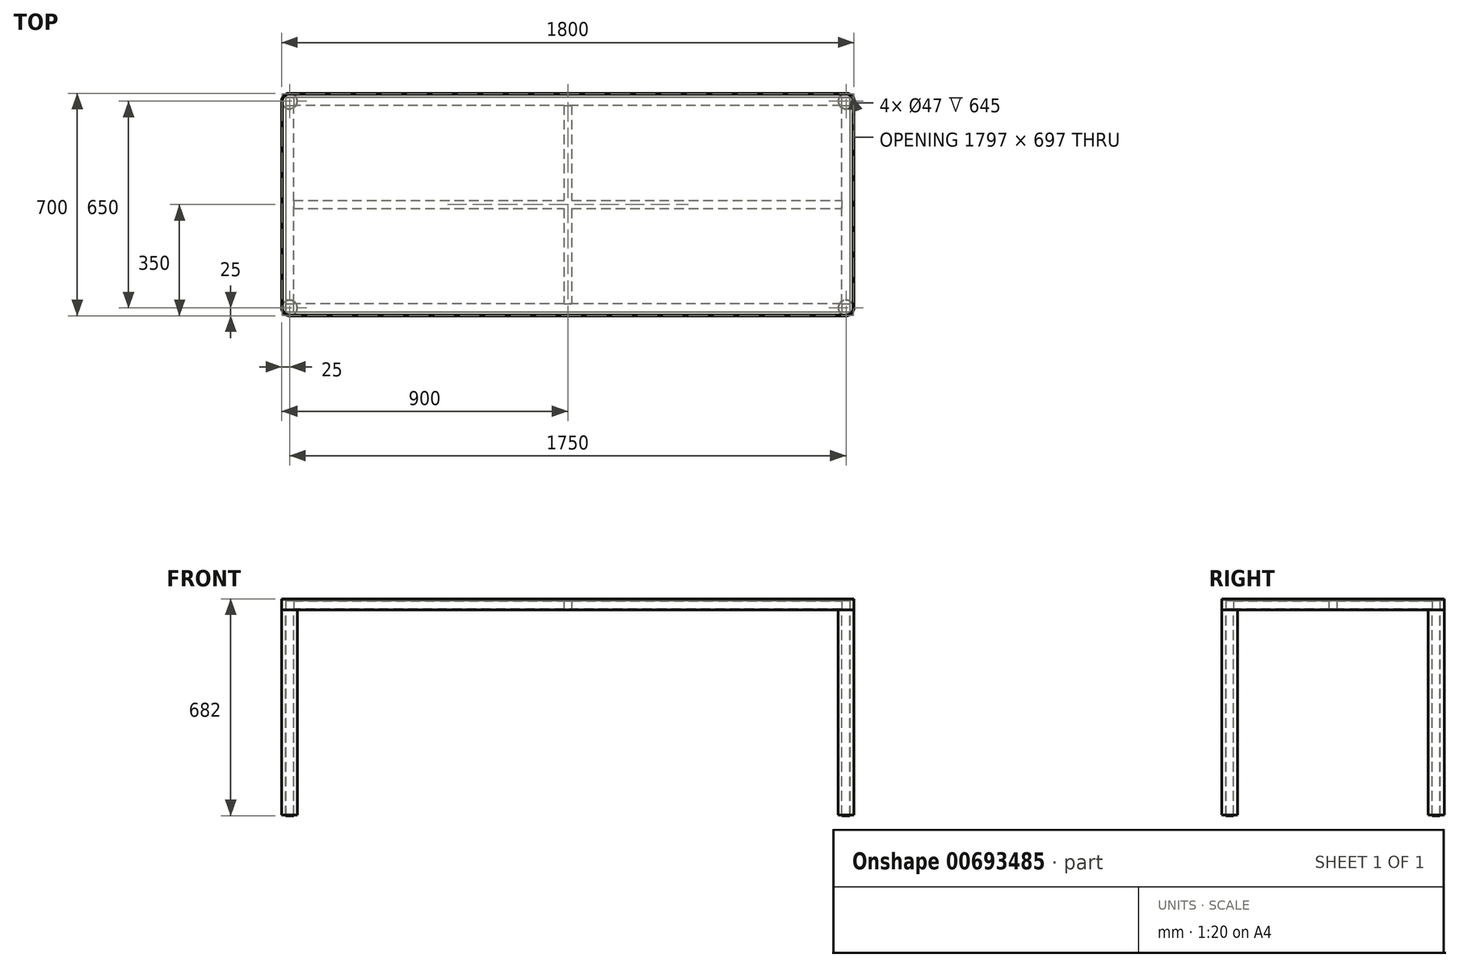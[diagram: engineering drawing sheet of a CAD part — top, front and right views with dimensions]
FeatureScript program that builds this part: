
annotation { "Feature Type Name" : "Feature", "Feature Type Description" : "" }
export const myFeature = defineFeature(function(context is Context, id is Id, definition is map)
    precondition{}
    {
        {
            var Q0;
            Q0=qCreatedBy(makeId("Top.planeOp"),FACE);
            var sketch = newSketch(context, id + "F0", { "sketchPlane" : qUnion([Q0])});
            skLineSegment(sketch, "E0.bottom", {"start": v(875, 350) * mm, "end": v(-875, 350) * mm});
            skLineSegment(sketch, "E0.top", {"start": v(875, -350) * mm, "end": v(-875, -350) * mm});
            skLineSegment(sketch, "E0.left", {"start": v(900, 325) * mm, "end": v(900, -325) * mm});
            skLineSegment(sketch, "E0.right", {"start": v(-900, 325) * mm, "end": v(-900, -325) * mm});
            skPoint(sketch, "E0.middle", {"position": v(0, 0) * mm});
            skLineSegment(sketch, "E1.bottom", {"start": v(-875, 350) * mm, "end": v(-850, 350) * mm});
            skLineSegment(sketch, "E1.top", {"start": v(-900, 300) * mm, "end": v(-898.5, 300) * mm});
            skLineSegment(sketch, "E1.left", {"start": v(-900, 325) * mm, "end": v(-900, 300) * mm});
            skArc(sketch, "E2", {"start": v(-875, 350) * mm, "mid": v(-892.68, 342.68) * mm, "end": v(-900, 325) * mm});
            skPoint(sketch, "E2.first.point", {"position": v(-875, 300) * mm});
            skPoint(sketch, "E2.second.point", {"position": v(-900, 325) * mm});
            skPoint(sketch, "E2.third.point", {"position": v(-875, 350) * mm});
            skArc(sketch, "E3.MirrorC", {"start": v(875, 350) * mm, "mid": v(892.68, 342.68) * mm, "end": v(900, 325) * mm});
            skArc(sketch, "E4.MirrorC", {"start": v(-875, -350) * mm, "mid": v(-892.68, -342.68) * mm, "end": v(-900, -325) * mm});
            skArc(sketch, "E5.MirrorC", {"start": v(875, -350) * mm, "mid": v(892.68, -342.68) * mm, "end": v(900, -325) * mm});
            skArc(sketch, "E6", {"start": v(-875, 348.5) * mm, "mid": v(-891.62, 341.62) * mm, "end": v(-898.5, 325) * mm});
            skArc(sketch, "E7.MirrorC", {"start": v(875, 348.5) * mm, "mid": v(891.62, 341.62) * mm, "end": v(898.5, 325) * mm});
            skArc(sketch, "E8.MirrorC", {"start": v(-875, -348.5) * mm, "mid": v(-891.62, -341.62) * mm, "end": v(-898.5, -325) * mm});
            skArc(sketch, "E9.MirrorC", {"start": v(875, -348.5) * mm, "mid": v(891.62, -341.62) * mm, "end": v(898.5, -325) * mm});
            skLineSegment(sketch, "E10", {"start": v(-898.5, -325) * mm, "end": v(-898.5, 325) * mm});
            skLineSegment(sketch, "E11", {"start": v(-875, 348.5) * mm, "end": v(875, 348.5) * mm});
            skLineSegment(sketch, "E12", {"start": v(898.5, 325) * mm, "end": v(898.5, -325) * mm});
            skLineSegment(sketch, "E13", {"start": v(875, -348.5) * mm, "end": v(-875, -348.5) * mm});
            skPoint(sketch, "E14.orphan", {"position": v(-900, -350) * mm});
            skPoint(sketch, "E15.orphan", {"position": v(-850, 300) * mm});
            skPoint(sketch, "E16.orphan", {"position": v(-900, 350) * mm});
            skPoint(sketch, "E17.orphan", {"position": v(900, -350) * mm});
            skPoint(sketch, "E18.orphan", {"position": v(900, 350) * mm});
            skSolve(sketch);
        }
        {
            var Q0;
            Q0=makeQuery(id+"F0.imprint","IMPRINT",FACE,{"disambiguationData":[TD([[makeQuery(id+"F0.imprint","IMPRINT",EDGE,{"derivedFrom":sQuery(id+"F0.wireOp",EDGE,"E0.bottom")}),1.0]])]});
            extrude(context, id + "F1", {"entities" : qUnion([Q0]), "oppositeDirection" : true, "depth" : 35 * mm, "offsetDistance" : 25 * mm});
        }
        {
            var Q0;
            Q0=qCreatedBy(makeId("Top.planeOp"),FACE);
            var sketch = newSketch(context, id + "F2", { "sketchPlane" : qUnion([Q0])});
            skArc(sketch, "E19", {"start": v(875, -347.5) * mm, "mid": v(890.9, -340.9) * mm, "end": v(897.5, -325) * mm});
            skArc(sketch, "E20", {"start": v(897.5, 325) * mm, "mid": v(890.9, 340.9) * mm, "end": v(875, 347.5) * mm});
            skLineSegment(sketch, "E21", {"start": v(897.5, 325) * mm, "end": v(897.5, -325) * mm});
            skLineSegment(sketch, "E22", {"start": v(875, -347.5) * mm, "end": v(-875, -347.5) * mm});
            skLineSegment(sketch, "E23", {"start": v(-897.5, -325) * mm, "end": v(-897.5, 325) * mm});
            skLineSegment(sketch, "E24", {"start": v(-875, 347.5) * mm, "end": v(875, 347.5) * mm});
            skArc(sketch, "E25", {"start": v(-897.5, 325) * mm, "mid": v(-890.9, 340.9) * mm, "end": v(-875, 347.5) * mm});
            skArc(sketch, "E26", {"start": v(-897.5, -325) * mm, "mid": v(-890.9, -340.9) * mm, "end": v(-875, -347.5) * mm});
            skSolve(sketch);
        }
        {
            var Q0;
            Q0=makeQuery(id+"F2.imprint","IMPRINT",FACE,{"disambiguationData":[TD([[makeQuery(id+"F2.imprint","IMPRINT",EDGE,{"derivedFrom":sQuery(id+"F2.wireOp",EDGE,"E19")}),1.0]])]});
            extrude(context, id + "F3", {"entities" : qUnion([Q0]), "oppositeDirection" : true, "depth" : 4 * mm, "offsetDistance" : 25 * mm});
        }
        {
            var Q0;
            Q0=makeQuery(id+"F1.opExtrude","CAP_FACE",FACE,{"disambiguationData":[OSD([sQuery(id+"F0.wireOp",EDGE,"E0.bottom"),sQuery(id+"F0.wireOp",EDGE,"E0.top"),sQuery(id+"F0.wireOp",EDGE,"E0.left"),sQuery(id+"F0.wireOp",EDGE,"E0.right"),sQuery(id+"F0.wireOp",EDGE,"E1.bottom"),sQuery(id+"F0.wireOp",EDGE,"E1.left"),sQuery(id+"F0.wireOp",EDGE,"E2"),sQuery(id+"F0.wireOp",EDGE,"E3.MirrorC"),sQuery(id+"F0.wireOp",EDGE,"E4.MirrorC"),sQuery(id+"F0.wireOp",EDGE,"E5.MirrorC"),sQuery(id+"F0.wireOp",EDGE,"E6"),sQuery(id+"F0.wireOp",EDGE,"E7.MirrorC"),sQuery(id+"F0.wireOp",EDGE,"E8.MirrorC"),sQuery(id+"F0.wireOp",EDGE,"E9.MirrorC"),sQuery(id+"F0.wireOp",EDGE,"E10"),sQuery(id+"F0.wireOp",EDGE,"E11"),sQuery(id+"F0.wireOp",EDGE,"E12"),sQuery(id+"F0.wireOp",EDGE,"E13")])],"isStart":false});
            cPlane(context, id + "F4", {"entities" : qUnion([Q0]), "cplaneType" : CPlaneType.OFFSET, "offset" : 3 * mm, "oppositeDirection" : true, "width" : 150 * mm, "height" : 150 * mm});
        }
        {
            var Q0;
            Q0=qCreatedBy(id+"F4.planeOp",FACE);
            var sketch = newSketch(context, id + "F5", { "sketchPlane" : qUnion([Q0])});
            skLineSegment(sketch, "E27.top", {"start": v(-875, -337) * mm, "end": v(-887, -337) * mm});
            skLineSegment(sketch, "E27.right", {"start": v(-887, -325) * mm, "end": v(-887, -337) * mm});
            skLineSegment(sketch, "E28.top", {"start": v(-875, 337) * mm, "end": v(-887, 337) * mm});
            skLineSegment(sketch, "E28.right", {"start": v(-887, 325) * mm, "end": v(-887, 337) * mm});
            skLineSegment(sketch, "E29.bottom", {"start": v(-887, -337) * mm, "end": v(887, -337) * mm});
            skLineSegment(sketch, "E29.top", {"start": v(-887, 337) * mm, "end": v(887, 337) * mm});
            skLineSegment(sketch, "E29.left", {"start": v(-887, -337) * mm, "end": v(-887, 337) * mm});
            skLineSegment(sketch, "E29.right", {"start": v(887, -337) * mm, "end": v(887, 337) * mm});
            skLineSegment(sketch, "E30.bottom", {"start": v(862, 312) * mm, "end": v(-862, 312) * mm});
            skLineSegment(sketch, "E30.top", {"start": v(862, -312) * mm, "end": v(-862, -312) * mm});
            skLineSegment(sketch, "E30.left", {"start": v(862, 312) * mm, "end": v(862, -312) * mm});
            skLineSegment(sketch, "E30.right", {"start": v(-862, 312) * mm, "end": v(-862, -312) * mm});
            skSolve(sketch);
        }
        {
            var Q0;
            {var subQ0=sQuery(id+"F5.wireOp",EDGE,"E29.right");Q0=makeQuery(id+"F5.imprint","IMPRINT",FACE,{"disambiguationData":[TD([[makeQuery(id+"F5.imprint","IMPRINT",EDGE,{"derivedFrom":subQ0}),1.0]])]});}
            extrude(context, id + "F6", {"entities" : qUnion([Q0]), "oppositeDirection" : true, "depth" : 25 * mm, "offsetDistance" : 25 * mm});
        }
        {
            var Q0;
            Q0=makeQuery(id+"F6.opExtrude","CAP_FACE",FACE,{"disambiguationData":[OSD([sQuery(id+"F5.wireOp",EDGE,"E29.bottom"),sQuery(id+"F5.wireOp",EDGE,"E29.top"),sQuery(id+"F5.wireOp",EDGE,"E29.left"),sQuery(id+"F5.wireOp",EDGE,"E29.right"),sQuery(id+"F5.wireOp",EDGE,"E30.bottom"),sQuery(id+"F5.wireOp",EDGE,"E30.top"),sQuery(id+"F5.wireOp",EDGE,"E30.left"),sQuery(id+"F5.wireOp",EDGE,"E30.right")])],"isStart":true});
            var sketch = newSketch(context, id + "F7", { "sketchPlane" : qUnion([Q0])});
            skArc(sketch, "E31.0", {"start": v(-875, -350) * mm, "mid": v(-892.68, -342.68) * mm, "end": v(-900, -325) * mm});
            skCircle(sketch, "E32", {"center": v(-875, -325) * mm, "radius": 25 * mm});
            skCircle(sketch, "E33", {"center": v(-875, -325) * mm, "radius": 4 * mm});
            skArc(sketch, "E34.0", {"start": v(-875, 350) * mm, "mid": v(-892.68, 342.68) * mm, "end": v(-900, 325) * mm});
            skCircle(sketch, "E35", {"center": v(-875, 325) * mm, "radius": 25 * mm});
            skArc(sketch, "E36.0", {"start": v(875, 350) * mm, "mid": v(892.68, 342.68) * mm, "end": v(900, 325) * mm});
            skCircle(sketch, "E37", {"center": v(875, 325) * mm, "radius": 25 * mm});
            skArc(sketch, "E38.0", {"start": v(875, -350) * mm, "mid": v(892.68, -342.68) * mm, "end": v(900, -325) * mm});
            skCircle(sketch, "E39", {"center": v(875, -325) * mm, "radius": 25 * mm});
            skCircle(sketch, "E40", {"center": v(875, -325) * mm, "radius": 4 * mm});
            skCircle(sketch, "E41", {"center": v(875, 325) * mm, "radius": 4 * mm});
            skCircle(sketch, "E42", {"center": v(-875, 325) * mm, "radius": 4 * mm});
            skSolve(sketch);
        }
        {
            var Q0;
            {var subQ0=sQuery(id+"F7.wireOp",EDGE,"E32");var subQ1=makeQuery(id+"F6.opExtrude","CAP_EDGE",EDGE,{"disambiguationData":[OSD([sQuery(id+"F5.wireOp",EDGE,"E29.left")])],"isStart":true});var subQ2=makeQuery(id+"F7.imprint","INTERSECT",VERTEX,{"derivedFrom":[subQ1,subQ0]});Q0=makeQuery(id+"F7.imprint","IMPRINT",FACE,{"disambiguationData":[TD([[makeQuery(id+"F7.imprint","IMPRINT",EDGE,{"disambiguationData":[TD([[subQ2,1.0]])],"derivedFrom":subQ0}),-1.0]])]});}
            var sketch = newSketch(context, id + "F8", { "sketchPlane" : qUnion([Q0])});
            skPoint(sketch, "E43.0", {"position": v(-887, -337) * mm});
            skPoint(sketch, "E44.0", {"position": v(-862, -312) * mm});
            skLineSegment(sketch, "E45.bottom", {"start": v(-887, -337) * mm, "end": v(-862, -337) * mm});
            skLineSegment(sketch, "E45.top", {"start": v(-887, -312) * mm, "end": v(-862, -312) * mm});
            skLineSegment(sketch, "E45.left", {"start": v(-887, -337) * mm, "end": v(-887, -312) * mm});
            skLineSegment(sketch, "E45.right", {"start": v(-862, -337) * mm, "end": v(-862, -312) * mm});
            skPoint(sketch, "E46.0", {"position": v(-887, 337) * mm});
            skPoint(sketch, "E47.0", {"position": v(-862, 312) * mm});
            skLineSegment(sketch, "E48.bottom", {"start": v(-887, 337) * mm, "end": v(-862, 337) * mm});
            skLineSegment(sketch, "E48.top", {"start": v(-887, 312) * mm, "end": v(-862, 312) * mm});
            skLineSegment(sketch, "E48.left", {"start": v(-887, 337) * mm, "end": v(-887, 312) * mm});
            skLineSegment(sketch, "E48.right", {"start": v(-862, 337) * mm, "end": v(-862, 312) * mm});
            skPoint(sketch, "E49.0", {"position": v(887, 337) * mm});
            skPoint(sketch, "E50.0", {"position": v(862, 312) * mm});
            skLineSegment(sketch, "E51.bottom", {"start": v(862, 312) * mm, "end": v(887, 312) * mm});
            skLineSegment(sketch, "E51.top", {"start": v(862, 337) * mm, "end": v(887, 337) * mm});
            skLineSegment(sketch, "E51.left", {"start": v(862, 312) * mm, "end": v(862, 337) * mm});
            skLineSegment(sketch, "E51.right", {"start": v(887, 312) * mm, "end": v(887, 337) * mm});
            skPoint(sketch, "E52.0", {"position": v(862, -312) * mm});
            skPoint(sketch, "E53.0", {"position": v(887, -337) * mm});
            skLineSegment(sketch, "E54.bottom", {"start": v(862, -312) * mm, "end": v(887, -312) * mm});
            skLineSegment(sketch, "E54.top", {"start": v(862, -337) * mm, "end": v(887, -337) * mm});
            skLineSegment(sketch, "E54.left", {"start": v(862, -312) * mm, "end": v(862, -337) * mm});
            skLineSegment(sketch, "E54.right", {"start": v(887, -312) * mm, "end": v(887, -337) * mm});
            skSolve(sketch);
        }
        {
            var Q0;
            Q0 = qSketchRegion(id + "F8", true);
            extrude(context, id + "F9", {"entities" : qUnion([Q0]), "operationType" : NewBodyOperationType.ADD, "depth" : 650 * mm, "offsetDistance" : 25 * mm});
        }
        {
            var Q0;
            Q0=makeQuery(id+"F1.opExtrude","CAP_FACE",FACE,{"disambiguationData":[OSD([sQuery(id+"F0.wireOp",EDGE,"E0.bottom"),sQuery(id+"F0.wireOp",EDGE,"E0.top"),sQuery(id+"F0.wireOp",EDGE,"E0.left"),sQuery(id+"F0.wireOp",EDGE,"E0.right"),sQuery(id+"F0.wireOp",EDGE,"E1.bottom"),sQuery(id+"F0.wireOp",EDGE,"E1.left"),sQuery(id+"F0.wireOp",EDGE,"E2"),sQuery(id+"F0.wireOp",EDGE,"E3.MirrorC"),sQuery(id+"F0.wireOp",EDGE,"E4.MirrorC"),sQuery(id+"F0.wireOp",EDGE,"E5.MirrorC"),sQuery(id+"F0.wireOp",EDGE,"E6"),sQuery(id+"F0.wireOp",EDGE,"E7.MirrorC"),sQuery(id+"F0.wireOp",EDGE,"E8.MirrorC"),sQuery(id+"F0.wireOp",EDGE,"E9.MirrorC"),sQuery(id+"F0.wireOp",EDGE,"E10"),sQuery(id+"F0.wireOp",EDGE,"E11"),sQuery(id+"F0.wireOp",EDGE,"E12"),sQuery(id+"F0.wireOp",EDGE,"E13")])],"isStart":false});
            cPlane(context, id + "F10", {"entities" : qUnion([Q0]), "cplaneType" : CPlaneType.OFFSET, "offset" : 0 * mm, "width" : 150 * mm, "height" : 150 * mm});
        }
        {
            var Q0;
            Q0=qCreatedBy(id+"F10.planeOp",FACE);
            var sketch = newSketch(context, id + "F11", { "sketchPlane" : qUnion([Q0])});
            skArc(sketch, "E55.0", {"start": v(-875, -350) * mm, "mid": v(-892.68, -342.68) * mm, "end": v(-900, -325) * mm});
            skCircle(sketch, "E56", {"center": v(-875, -325) * mm, "radius": 25 * mm});
            skCircle(sketch, "E57", {"center": v(-875, -325) * mm, "radius": 23.5 * mm});
            skArc(sketch, "E58.MirrorCS", {"start": v(875, -350) * mm, "mid": v(892.68, -342.68) * mm, "end": v(900, -325) * mm});
            skCircle(sketch, "E59.MirrorC", {"center": v(875, -325) * mm, "radius": 23.5 * mm});
            skCircle(sketch, "E60.MirrorC", {"center": v(875, -325) * mm, "radius": 25 * mm});
            skArc(sketch, "E61.MirrorCS", {"start": v(-875, 350) * mm, "mid": v(-892.68, 342.68) * mm, "end": v(-900, 325) * mm});
            skArc(sketch, "E62.MirrorCS", {"start": v(875, 350) * mm, "mid": v(892.68, 342.68) * mm, "end": v(900, 325) * mm});
            skCircle(sketch, "E63.MirrorC", {"center": v(875, 325) * mm, "radius": 23.5 * mm});
            skCircle(sketch, "E64.MirrorC", {"center": v(-875, 325) * mm, "radius": 23.5 * mm});
            skCircle(sketch, "E65.MirrorC", {"center": v(875, 325) * mm, "radius": 25 * mm});
            skCircle(sketch, "E66.MirrorC", {"center": v(-875, 325) * mm, "radius": 25 * mm});
            skSolve(sketch);
        }
        {
            var Q0;
            Q0 = qSketchRegion(id + "F11", true);
            extrude(context, id + "F12", {"entities" : qUnion([Q0]), "depth" : 645 * mm, "offsetDistance" : 25 * mm});
        }
        {
            var Q0;
            Q0=qCreatedBy(id+"F4.planeOp",FACE);
            var sketch = newSketch(context, id + "F13", { "sketchPlane" : qUnion([Q0])});
            skLineSegment(sketch, "E67.0", {"start": v(862, 312) * mm, "end": v(-862, 312) * mm});
            skLineSegment(sketch, "E68.0", {"start": v(862, -312) * mm, "end": v(-862, -312) * mm});
            skLineSegment(sketch, "E69", {"start": v(0, -312) * mm, "end": v(0, 312) * mm});
            skLineSegment(sketch, "E70.0", {"start": v(-862, 312) * mm, "end": v(-862, -312) * mm});
            skLineSegment(sketch, "E71.0", {"start": v(862, 312) * mm, "end": v(862, -312) * mm});
            skLineSegment(sketch, "E72", {"start": v(-862, 0) * mm, "end": v(862, 0) * mm});
            skLineSegment(sketch, "E73", {"start": v(-862, 0) * mm, "end": v(-862, -12.5) * mm});
            skLineSegment(sketch, "E74", {"start": v(862, 0) * mm, "end": v(862, 12.5) * mm});
            skLineSegment(sketch, "E75.bottom", {"start": v(-862, -12.5) * mm, "end": v(862, -12.5) * mm});
            skLineSegment(sketch, "E75.top", {"start": v(-862, 12.5) * mm, "end": v(862, 12.5) * mm});
            skLineSegment(sketch, "E75.left", {"start": v(-862, -12.5) * mm, "end": v(-862, 12.5) * mm});
            skLineSegment(sketch, "E75.right", {"start": v(862, -12.5) * mm, "end": v(862, 12.5) * mm});
            skLineSegment(sketch, "E76", {"start": v(0, 312) * mm, "end": v(12.5, 312) * mm});
            skLineSegment(sketch, "E77", {"start": v(0, -312) * mm, "end": v(-12.5, -312) * mm});
            skLineSegment(sketch, "E78.bottom", {"start": v(-12.5, -312) * mm, "end": v(12.5, -312) * mm});
            skLineSegment(sketch, "E78.top", {"start": v(-12.5, 312) * mm, "end": v(12.5, 312) * mm});
            skLineSegment(sketch, "E78.left", {"start": v(-12.5, -312) * mm, "end": v(-12.5, 312) * mm});
            skLineSegment(sketch, "E78.right", {"start": v(12.5, -312) * mm, "end": v(12.5, 312) * mm});
            skSolve(sketch);
        }
        {
            var Q0;
            Q0=qCreatedBy(id+"F4.planeOp",FACE);
            var sketch = newSketch(context, id + "F14", { "sketchPlane" : qUnion([Q0])});
            skLineSegment(sketch, "E79.0", {"start": v(-862, -12.5) * mm, "end": v(-12.5, -12.5) * mm});
            skLineSegment(sketch, "E80.0", {"start": v(-862, 12.5) * mm, "end": v(-12.5, 12.5) * mm});
            skLineSegment(sketch, "E81.0", {"start": v(-12.5, -312) * mm, "end": v(-12.5, -12.5) * mm});
            skLineSegment(sketch, "E82.0", {"start": v(12.5, -312) * mm, "end": v(12.5, -12.5) * mm});
            skLineSegment(sketch, "E83", {"start": v(-862, -12.5) * mm, "end": v(-862, 12.5) * mm});
            skLineSegment(sketch, "E84", {"start": v(-12.5, 312) * mm, "end": v(12.5, 312) * mm});
            skLineSegment(sketch, "E85", {"start": v(-12.5, -312) * mm, "end": v(12.5, -312) * mm});
            skLineSegment(sketch, "E86", {"start": v(862, -12.5) * mm, "end": v(862, 12.5) * mm});
            skLineSegment(sketch, "E87.trimOffspring", {"start": v(-12.5, 12.5) * mm, "end": v(-12.5, 312) * mm});
            skLineSegment(sketch, "E88.trimOffspring", {"start": v(12.5, 12.5) * mm, "end": v(862, 12.5) * mm});
            skLineSegment(sketch, "E89.trimOffspring", {"start": v(12.5, 12.5) * mm, "end": v(12.5, 312) * mm});
            skLineSegment(sketch, "E90.trimOffspring", {"start": v(12.5, -12.5) * mm, "end": v(862, -12.5) * mm});
            skSolve(sketch);
        }
        {
            var Q0;
            Q0=makeQuery(id+"F14.imprint","IMPRINT",FACE,{"disambiguationData":[TD([[makeQuery(id+"F14.imprint","IMPRINT",EDGE,{"derivedFrom":sQuery(id+"F14.wireOp",EDGE,"E79.0")}),1.0]])]});
            extrude(context, id + "F15", {"entities" : qUnion([Q0]), "oppositeDirection" : true, "depth" : 25 * mm, "offsetDistance" : 25 * mm});
        }
    });
